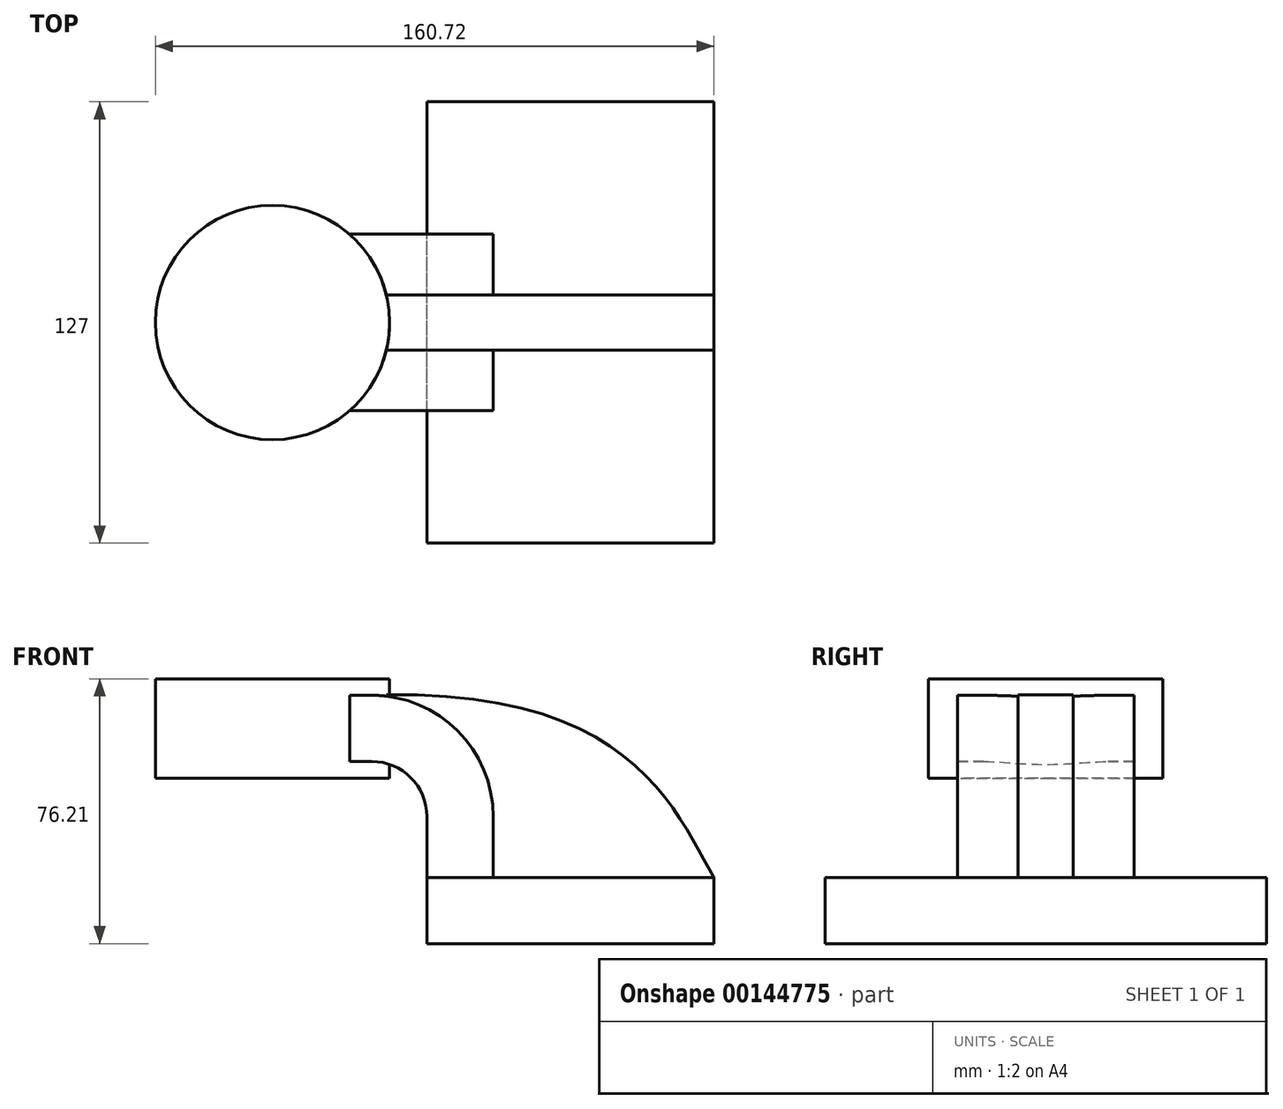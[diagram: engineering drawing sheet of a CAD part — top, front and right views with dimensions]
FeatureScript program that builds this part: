
annotation { "Feature Type Name" : "Feature", "Feature Type Description" : "" }
export const myFeature = defineFeature(function(context is Context, id is Id, definition is map)
    precondition{}
    {
        {
            var Q0;
            Q0=qCreatedBy(makeId("Front.planeOp"),FACE);
            var sketch = newSketch(context, id + "F0", { "sketchPlane" : qUnion([Q0])});
            skLineSegment(sketch, "E0.bottom", {"start": v(-41.28, -9.53) * mm, "end": v(41.28, -9.53) * mm});
            skLineSegment(sketch, "E0.top", {"start": v(-41.28, 9.52) * mm, "end": v(41.28, 9.52) * mm});
            skLineSegment(sketch, "E0.left", {"start": v(-41.28, -9.53) * mm, "end": v(-41.28, 9.52) * mm});
            skLineSegment(sketch, "E0.right", {"start": v(41.28, -9.53) * mm, "end": v(41.28, 9.52) * mm});
            skPoint(sketch, "E0.middle", {"position": v(0, 0) * mm});
            skLineSegment(sketch, "E1.bottom", {"start": v(-68.64, 66.67) * mm, "end": v(-119.44, 66.67) * mm});
            skLineSegment(sketch, "E1.top", {"start": v(-68.64, 38.1) * mm, "end": v(-119.44, 38.1) * mm});
            skLineSegment(sketch, "E1.left", {"start": v(-68.64, 66.67) * mm, "end": v(-68.64, 38.1) * mm});
            skLineSegment(sketch, "E1.right", {"start": v(-119.44, 66.67) * mm, "end": v(-119.44, 38.1) * mm});
            skLineSegment(sketch, "E2", {"start": v(-41.28, 9.52) * mm, "end": v(-41.28, 27) * mm});
            skArc(sketch, "E3", {"start": v(-41.28, 27) * mm, "mid": v(-45.92, 38.23) * mm, "end": v(-57.15, 42.88) * mm});
            skLineSegment(sketch, "E4", {"start": v(-57.15, 42.88) * mm, "end": v(-85.73, 42.88) * mm});
            skLineSegment(sketch, "E5.0", {"start": v(-57.15, 61.93) * mm, "end": v(-85.73, 61.93) * mm});
            skArc(sketch, "E5.1", {"start": v(-22.23, 27) * mm, "mid": v(-32.45, 51.7) * mm, "end": v(-57.15, 61.93) * mm});
            skLineSegment(sketch, "E5.2", {"start": v(-22.23, 9.52) * mm, "end": v(-22.23, 27) * mm});
            skLineSegment(sketch, "E6", {"start": v(-85.73, 38.1) * mm, "end": v(-85.73, 66.67) * mm});
            skFitSpline(sketch, "E7", {"points": [v(41.28, 9.52) * mm, v(-57.15, 61.93) * mm], "startDerivative": vector(-32.93, 56.04) * mm, "endDerivative": vector(-225.28, -8.52) * mm});
            skSolve(sketch);
        }
        {
            var Q0;
            Q0=makeQuery(id+"F0.imprint","IMPRINT",FACE,{"disambiguationData":[TD([[makeQuery(id+"F0.imprint","IMPRINT",EDGE,{"derivedFrom":sQuery(id+"F0.wireOp",EDGE,"E0.bottom")}),1.0]])]});
            extrude(context, id + "F1", {"entities" : qUnion([Q0]), "endBound" : BoundingType.SYMMETRIC, "depth" : 127 * mm});
        }
        {
            var Q0;
            {var subQ0=sQuery(id+"F0.wireOp",EDGE,"E5.0");var subQ1=sQuery(id+"F0.wireOp",EDGE,"E1.left");var subQ2=makeQuery(id+"F0.imprint","INTERSECT",VERTEX,{"derivedFrom":[subQ1,subQ0]});Q0=makeQuery(id+"F0.imprint","IMPRINT",FACE,{"disambiguationData":[TD([[makeQuery(id+"F0.imprint","IMPRINT",EDGE,{"disambiguationData":[TD([[subQ2,-1.0]])],"derivedFrom":subQ1}),-1.0]])]});}
            var Q1;
            {var subQ1=sQuery(id+"F0.wireOp",EDGE,"E2");Q1=makeQuery(id+"F0.imprint","IMPRINT",FACE,{"disambiguationData":[TD([[makeQuery(id+"F0.imprint","IMPRINT",EDGE,{"derivedFrom":subQ1}),-1.0]])]});}
            extrude(context, id + "F2", {"entities" : qUnion([Q0, Q1]), "operationType" : NewBodyOperationType.ADD, "endBound" : BoundingType.SYMMETRIC, "depth" : 50.8 * mm});
        }
        {
            var Q0;
            Q0=makeQuery(id+"F0.imprint","IMPRINT",FACE,{"disambiguationData":[TD([[makeQuery(id+"F0.imprint","IMPRINT",EDGE,{"derivedFrom":sQuery(id+"F0.wireOp",EDGE,"E5.1")}),-1.0]])]});
            extrude(context, id + "F3", {"entities" : qUnion([Q0]), "operationType" : NewBodyOperationType.ADD, "endBound" : BoundingType.SYMMETRIC, "depth" : 15.88 * mm});
        }
        {
            var Q0;
            {var subQ0=sQuery(id+"F0.wireOp",EDGE,"E1.right");Q0=makeQuery(id+"F0.imprint","IMPRINT",FACE,{"disambiguationData":[TD([[makeQuery(id+"F0.imprint","IMPRINT",EDGE,{"derivedFrom":subQ0}),1.0]])]});}
            var Q1;
            Q1=sQuery(id+"F0.wireOp",EDGE,"E6");
            revolve(context, id + "F4", {"operationType" : NewBodyOperationType.ADD, "entities" : qUnion([Q0]), "axis" : qUnion([Q1]), "revolveType" : RevolveType.FULL});
        }
    });
